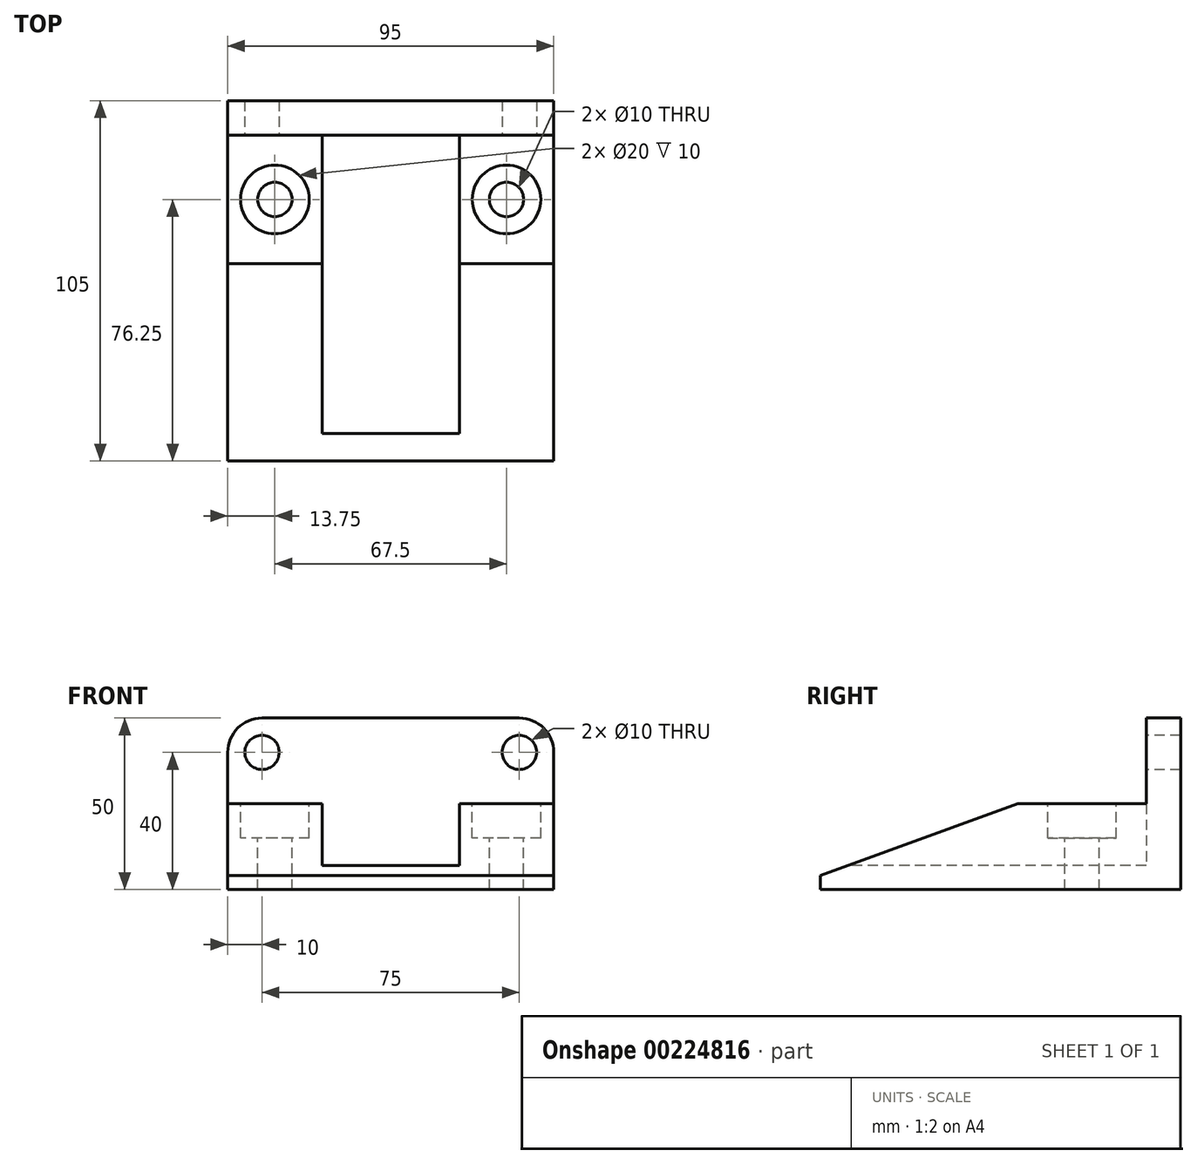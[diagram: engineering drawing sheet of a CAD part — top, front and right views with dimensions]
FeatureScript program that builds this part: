
annotation { "Feature Type Name" : "Feature", "Feature Type Description" : "" }
export const myFeature = defineFeature(function(context is Context, id is Id, definition is map)
    precondition{}
    {
        {
            var Q0;
            Q0=qCreatedBy(makeId("Front.planeOp"),FACE);
            var sketch = newSketch(context, id + "F0", { "sketchPlane" : qUnion([Q0])});
            skLineSegment(sketch, "E0.bottom", {"start": v(47.5, -25) * mm, "end": v(-47.5, -25) * mm});
            skLineSegment(sketch, "E0.top", {"start": v(47.5, 25) * mm, "end": v(-47.5, 25) * mm});
            skLineSegment(sketch, "E0.left", {"start": v(47.5, -25) * mm, "end": v(47.5, 25) * mm});
            skLineSegment(sketch, "E0.right", {"start": v(-47.5, -25) * mm, "end": v(-47.5, 25) * mm});
            skPoint(sketch, "E0.middle", {"position": v(0, 0) * mm});
            skLineSegment(sketch, "E1", {"start": v(0, 25) * mm, "end": v(0, -25) * mm, "construction": true});
            skSolve(sketch);
        }
        {
            var Q0;
            Q0=makeQuery(id+"F0.imprint","IMPRINT",FACE,{"disambiguationData":[TD([[makeQuery(id+"F0.imprint","IMPRINT",EDGE,{"derivedFrom":sQuery(id+"F0.wireOp",EDGE,"E0.bottom")}),-1.0]])]});
            extrude(context, id + "F1", {"entities" : qUnion([Q0]), "oppositeDirection" : true, "depth" : 10 * mm});
        }
        {
            var Q0;
            Q0=makeQuery(id+"F1.opExtrude","SWEPT_EDGE",EDGE,{"disambiguationData":[OSD([sQuery(id+"F0.wireOp",EDGE,"E0.top"),sQuery(id+"F0.wireOp",EDGE,"E0.right")])]});
            var Q1;
            Q1=makeQuery(id+"F1.opExtrude","SWEPT_EDGE",EDGE,{"disambiguationData":[OSD([sQuery(id+"F0.wireOp",EDGE,"E0.top"),sQuery(id+"F0.wireOp",EDGE,"E0.left")])]});
            fillet(context, id + "F2", {"entities" : qUnion([Q0, Q1]), "radius" : 10 * mm, "tangentPropagation" : true, "allowEdgeOverflow" : false});
        }
        {
            var Q0;
            Q0=makeQuery(id+"F0.imprint","IMPRINT",FACE,{"disambiguationData":[TD([[makeQuery(id+"F0.imprint","IMPRINT",EDGE,{"derivedFrom":sQuery(id+"F0.wireOp",EDGE,"E0.bottom")}),-1.0]])]});
            var sketch = newSketch(context, id + "F3", { "sketchPlane" : qUnion([Q0])});
            skArc(sketch, "E2.0", {"start": v(-37.5, 25) * mm, "mid": v(-44.57, 22.07) * mm, "end": v(-47.5, 15) * mm});
            skArc(sketch, "E2.1", {"start": v(47.5, 15) * mm, "mid": v(44.57, 22.07) * mm, "end": v(37.5, 25) * mm});
            skCircle(sketch, "E3", {"center": v(-37.5, 15) * mm, "radius": 5 * mm});
            skCircle(sketch, "E4", {"center": v(37.5, 15) * mm, "radius": 5 * mm});
            skLineSegment(sketch, "E5.0", {"start": v(47.5, 25) * mm, "end": v(-47.5, 25) * mm});
            skLineSegment(sketch, "E6.0", {"start": v(-47.5, -25) * mm, "end": v(-47.5, 25) * mm});
            skLineSegment(sketch, "E7.0", {"start": v(47.5, -25) * mm, "end": v(-47.5, -25) * mm});
            skLineSegment(sketch, "E8.0", {"start": v(47.5, -25) * mm, "end": v(47.5, 25) * mm});
            skLineSegment(sketch, "E9.bottom", {"start": v(-47.5, 0) * mm, "end": v(47.5, 0) * mm});
            skLineSegment(sketch, "E9.top", {"start": v(-47.5, -25) * mm, "end": v(47.5, -25) * mm});
            skLineSegment(sketch, "E9.left", {"start": v(-47.5, 0) * mm, "end": v(-47.5, -25) * mm});
            skLineSegment(sketch, "E9.right", {"start": v(47.5, 0) * mm, "end": v(47.5, -25) * mm});
            skSolve(sketch);
        }
        {
            var Q0;
            Q0=makeQuery(id+"F3.imprint","IMPRINT",FACE,{"disambiguationData":[TD([[makeQuery(id+"F3.imprint","IMPRINT",EDGE,{"derivedFrom":sQuery(id+"F3.wireOp",EDGE,"E3")}),1.0]])]});
            var Q1;
            Q1=makeQuery(id+"F3.imprint","IMPRINT",FACE,{"disambiguationData":[TD([[makeQuery(id+"F3.imprint","IMPRINT",EDGE,{"derivedFrom":sQuery(id+"F3.wireOp",EDGE,"E4")}),1.0]])]});
            extrude(context, id + "F4", {"entities" : qUnion([Q0, Q1]), "operationType" : NewBodyOperationType.REMOVE, "endBound" : BoundingType.UP_TO_NEXT, "oppositeDirection" : true, "depth" : 25 * mm});
        }
        {
            var Q0;
            Q0=makeQuery(id+"F3.imprint","IMPRINT",FACE,{"disambiguationData":[TD([[makeQuery(id+"F3.imprint","IMPRINT",EDGE,{"derivedFrom":sQuery(id+"F3.wireOp",EDGE,"E9.bottom")}),-1.0]])]});
            extrude(context, id + "F5", {"entities" : qUnion([Q0]), "operationType" : NewBodyOperationType.ADD, "depth" : 95 * mm});
        }
        {
            var Q0;
            Q0=makeQuery(id+"F5.opExtrude","CAP_FACE",FACE,{"disambiguationData":[OSD([sQuery(id+"F3.wireOp",EDGE,"E9.bottom"),sQuery(id+"F3.wireOp",EDGE,"E9.top"),sQuery(id+"F3.wireOp",EDGE,"E9.left"),sQuery(id+"F3.wireOp",EDGE,"E9.right")])],"isStart":false});
            var sketch = newSketch(context, id + "F6", { "sketchPlane" : qUnion([Q0])});
            skLineSegment(sketch, "E10.bottom", {"start": v(20, -18) * mm, "end": v(-20, -18) * mm});
            skLineSegment(sketch, "E10.top", {"start": v(20, 18) * mm, "end": v(-20, 18) * mm});
            skLineSegment(sketch, "E10.left", {"start": v(20, -18) * mm, "end": v(20, 18) * mm});
            skLineSegment(sketch, "E10.right", {"start": v(-20, -18) * mm, "end": v(-20, 18) * mm});
            skPoint(sketch, "E10.middle", {"position": v(0, 0) * mm});
            skSolve(sketch);
        }
        {
            var Q0;
            {var subQ0=sQuery(id+"F6.wireOp",EDGE,"E10.bottom");Q0=makeQuery(id+"F6.imprint","IMPRINT",FACE,{"disambiguationData":[TD([[makeQuery(id+"F6.imprint","IMPRINT",EDGE,{"derivedFrom":subQ0}),-1.0]])]});}
            var Q1;
            {var subQ0=sQuery(id+"F6.wireOp",EDGE,"E10.top");Q1=makeQuery(id+"F6.imprint","IMPRINT",FACE,{"disambiguationData":[TD([[makeQuery(id+"F6.imprint","IMPRINT",EDGE,{"derivedFrom":subQ0}),1.0]])]});}
            var Q2;
            Q2=makeQuery(id+"F1.opExtrude","CAP_FACE",FACE,{"disambiguationData":[OSD([sQuery(id+"F0.wireOp",EDGE,"E0.bottom"),sQuery(id+"F0.wireOp",EDGE,"E0.top"),sQuery(id+"F0.wireOp",EDGE,"E0.left"),sQuery(id+"F0.wireOp",EDGE,"E0.right")])],"isStart":true});
            extrude(context, id + "F7", {"entities" : qUnion([Q0, Q1]), "operationType" : NewBodyOperationType.REMOVE, "endBound" : BoundingType.UP_TO_SURFACE, "oppositeDirection" : true, "endBoundEntityFace" : qUnion([Q2]), "depth" : 25 * mm});
        }
        {
            var Q0;
            {var subQ1=sQuery(id+"F3.wireOp",EDGE,"E9.bottom");Q0=makeQuery(id+"F7.boolean.opBoolean","SPLIT",EDGE,{"disambiguationData":[TD([makeQuery(id+"F1.opExtrude","SWEPT_FACE",FACE,{"disambiguationData":[OSD([sQuery(id+"F0.wireOp",EDGE,"E0.right")])]})])],"derivedFrom":makeQuery(id+"F5.opExtrude","CAP_EDGE",EDGE,{"disambiguationData":[OSD([subQ1])],"isStart":false})});}
            var Q1;
            {var subQ1=sQuery(id+"F3.wireOp",EDGE,"E9.bottom");Q1=makeQuery(id+"F7.boolean.opBoolean","SPLIT",EDGE,{"disambiguationData":[TD([makeQuery(id+"F1.opExtrude","SWEPT_FACE",FACE,{"disambiguationData":[OSD([sQuery(id+"F0.wireOp",EDGE,"E0.left")])]})])],"derivedFrom":makeQuery(id+"F5.opExtrude","CAP_EDGE",EDGE,{"disambiguationData":[OSD([subQ1])],"isStart":false})});}
            chamfer(context, id + "F8", {"entities" : qUnion([Q0, Q1]), "chamferType" : ChamferType.OFFSET_ANGLE, "width" : 57.5 * mm, "oppositeDirection" : false, "angle" : 20 * degree, "tangentPropagation" : true});
        }
        {
            var Q0;
            {var subQ1=sQuery(id+"F0.wireOp",EDGE,"E0.right");var subQ5=sQuery(id+"F3.wireOp",EDGE,"E9.bottom");Q0=makeQuery(id+"F7.boolean.opBoolean","SPLIT",FACE,{"disambiguationData":[TD([makeQuery(id+"F1.opExtrude","SWEPT_FACE",FACE,{"disambiguationData":[OSD([subQ1])]})])],"derivedFrom":makeQuery(id+"F5.opExtrude","SWEPT_FACE",FACE,{"disambiguationData":[OSD([subQ5])]})});}
            var sketch = newSketch(context, id + "F9", { "sketchPlane" : qUnion([Q0])});
            skLineSegment(sketch, "E11.0.0", {"start": v(20, 0) * mm, "end": v(20, -37.5) * mm});
            skLineSegment(sketch, "E11.0.1", {"start": v(20, -37.5) * mm, "end": v(47.5, -37.5) * mm});
            skLineSegment(sketch, "E11.0.2", {"start": v(47.5, -37.5) * mm, "end": v(47.5, 0) * mm});
            skLineSegment(sketch, "E11.0.3", {"start": v(47.5, 0) * mm, "end": v(20, 0) * mm});
            skLineSegment(sketch, "E12.0.0", {"start": v(-47.5, 0) * mm, "end": v(-47.5, -37.5) * mm});
            skLineSegment(sketch, "E12.0.1", {"start": v(-47.5, -37.5) * mm, "end": v(-20, -37.5) * mm});
            skLineSegment(sketch, "E12.0.2", {"start": v(-20, -37.5) * mm, "end": v(-20, 0) * mm});
            skLineSegment(sketch, "E12.0.3", {"start": v(-20, 0) * mm, "end": v(-47.5, 0) * mm});
            skPoint(sketch, "E13", {"position": v(-33.75, -18.75) * mm});
            skPoint(sketch, "E13.positionSnap0", {"position": v(-20, -18.75) * mm});
            skPoint(sketch, "E13.positionSnap1", {"position": v(-33.75, 0) * mm});
            skPoint(sketch, "E14", {"position": v(33.75, -18.75) * mm});
            skPoint(sketch, "E14.positionSnap0", {"position": v(20, -18.75) * mm});
            skPoint(sketch, "E14.positionSnap1", {"position": v(33.75, 0) * mm});
            skSolve(sketch);
        }
        {
            var Q0;
            Q0=sQuery(id+"F9.wireOp",VERTEX,"E13");
            var Q1;
            Q1=sQuery(id+"F9.wireOp",VERTEX,"E14");
            var Q2;
            Q2=makeQuery(id+"F1.opExtrude","SWEPT_BODY",BODY,{"disambiguationData":[OSD([sQuery(id+"F0.wireOp",EDGE,"E0.bottom"),sQuery(id+"F0.wireOp",EDGE,"E0.top"),sQuery(id+"F0.wireOp",EDGE,"E0.left"),sQuery(id+"F0.wireOp",EDGE,"E0.right")])]});
            hole(context, id + "F10", {"style" : HoleStyle.C_BORE, "endStyle" : HoleEndStyle.THROUGH, "holeDiameter" : 10 * mm, "cBoreDiameter" : 20 * mm, "cBoreDepth" : 10 * mm, "locations" : qUnion([Q0, Q1]), "scope" : qUnion([Q2]), "isTappedThrough" : true});
        }
    });
